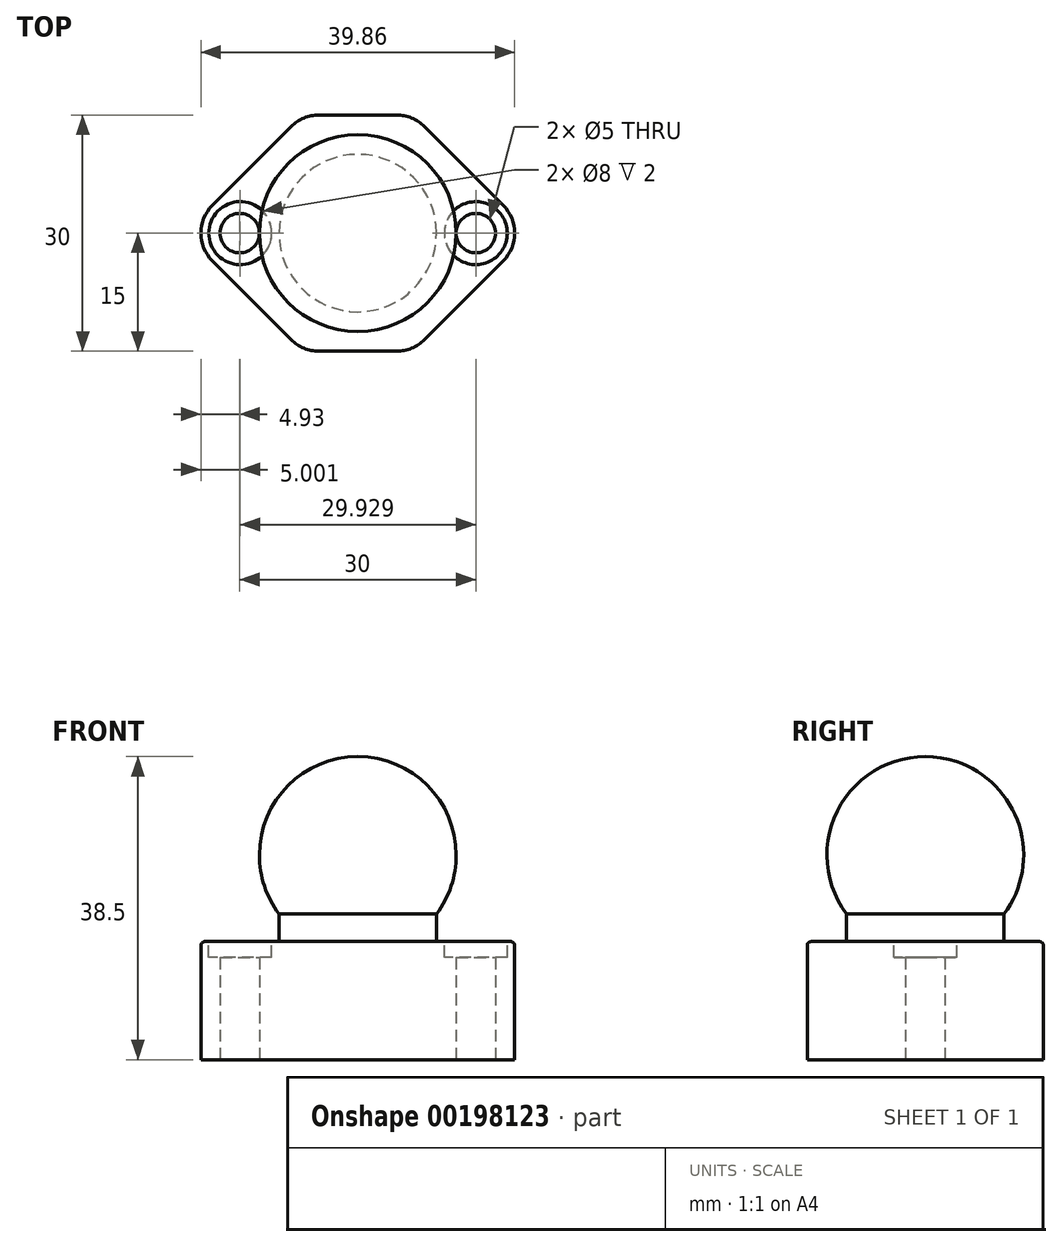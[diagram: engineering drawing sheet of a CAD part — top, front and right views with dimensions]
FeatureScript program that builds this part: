
annotation { "Feature Type Name" : "Feature", "Feature Type Description" : "" }
export const myFeature = defineFeature(function(context is Context, id is Id, definition is map)
    precondition{}
    {
        {
            var Q0;
            Q0=qCreatedBy(makeId("Top.planeOp"),FACE);
            var sketch = newSketch(context, id + "F0", { "sketchPlane" : qUnion([Q0])});
            skCircle(sketch, "E0", {"center": v(0, 0) * mm, "radius": 12.5 * mm});
            skLineSegment(sketch, "E1", {"start": v(22.5, 0) * mm, "end": v(-12.5, 0) * mm});
            skSolve(sketch);
        }
        {
            var Q0;
            {var subQ0=sQuery(id+"F0.wireOp",EDGE,"E1");var subQ1=sQuery(id+"F0.wireOp",EDGE,"E0");var subQ2=makeQuery(id+"F0.imprint","INTERSECT",VERTEX,{"disambiguationData":[OD(0.0)],"derivedFrom":[subQ1,subQ0]});Q0=makeQuery(id+"F0.imprint","IMPRINT",FACE,{"disambiguationData":[TD([[makeQuery(id+"F0.imprint","IMPRINT",EDGE,{"disambiguationData":[TD([[subQ2,1.0]])],"derivedFrom":subQ1}),1.0]])]});}
            var Q1;
            Q1=sQuery(id+"F0.wireOp",EDGE,"E1");
            revolve(context, id + "F1", {"entities" : qUnion([Q0]), "axis" : qUnion([Q1]), "revolveType" : RevolveType.FULL});
        }
        {
            var Q0;
            Q0=qCreatedBy(makeId("Top.planeOp"),FACE);
            var sketch = newSketch(context, id + "F2", { "sketchPlane" : qUnion([Q0])});
            skCircle(sketch, "E2", {"center": v(0, 0) * mm, "radius": 10 * mm});
            skSolve(sketch);
        }
        {
            var Q0;
            Q0 = qSketchRegion(id + "F2", true);
            extrude(context, id + "F3", {"entities" : qUnion([Q0]), "operationType" : NewBodyOperationType.ADD, "oppositeDirection" : true, "depth" : 26 * mm});
        }
        {
            var Q0;
            Q0=makeQuery(id+"F3.opExtrude","CAP_FACE",FACE,{"disambiguationData":[OSD([sQuery(id+"F2.wireOp",EDGE,"E2")])],"isStart":false});
            var sketch = newSketch(context, id + "F4", { "sketchPlane" : qUnion([Q0])});
            skLineSegment(sketch, "E3", {"start": v(0, 15) * mm, "end": v(7, 15) * mm});
            skLineSegment(sketch, "E4", {"start": v(7, 15) * mm, "end": v(22, 0) * mm});
            skLineSegment(sketch, "E5", {"start": v(0, 15) * mm, "end": v(-7, 15) * mm});
            skLineSegment(sketch, "E6", {"start": v(-7, 15) * mm, "end": v(-22, 0) * mm});
            skLineSegment(sketch, "E7", {"start": v(-22, 0) * mm, "end": v(-7, -15) * mm});
            skLineSegment(sketch, "E8", {"start": v(-7, -15) * mm, "end": v(0, -15) * mm});
            skLineSegment(sketch, "E9", {"start": v(7, -15) * mm, "end": v(22, 0) * mm});
            skLineSegment(sketch, "E10", {"start": v(7, -15) * mm, "end": v(0, -15) * mm});
            skCircle(sketch, "E11", {"center": v(15, 0) * mm, "radius": 2.5 * mm});
            skCircle(sketch, "E12", {"center": v(-15, 0) * mm, "radius": 2.5 * mm});
            skSolve(sketch);
        }
        {
            var Q0;
            Q0=makeQuery(id+"F4.imprint","IMPRINT",FACE,{"disambiguationData":[TD([[makeQuery(id+"F4.imprint","IMPRINT",EDGE,{"derivedFrom":sQuery(id+"F4.wireOp",EDGE,"E3")}),-1.0]])]});
            extrude(context, id + "F5", {"entities" : qUnion([Q0]), "operationType" : NewBodyOperationType.ADD, "oppositeDirection" : true, "depth" : 15 * mm});
        }
        {
            var Q0;
            Q0=makeQuery(id+"F5.opExtrude","SWEPT_EDGE",EDGE,{"disambiguationData":[OSD([sQuery(id+"F4.wireOp",EDGE,"E6"),sQuery(id+"F4.wireOp",EDGE,"E7")])]});
            var Q1;
            Q1=makeQuery(id+"F5.opExtrude","SWEPT_EDGE",EDGE,{"disambiguationData":[OSD([sQuery(id+"F4.wireOp",EDGE,"E5"),sQuery(id+"F4.wireOp",EDGE,"E6")])]});
            var Q2;
            Q2=makeQuery(id+"F5.opExtrude","SWEPT_EDGE",EDGE,{"disambiguationData":[OSD([sQuery(id+"F4.wireOp",EDGE,"E3"),sQuery(id+"F4.wireOp",EDGE,"E4")])]});
            var Q3;
            Q3=makeQuery(id+"F5.opExtrude","SWEPT_EDGE",EDGE,{"disambiguationData":[OSD([sQuery(id+"F4.wireOp",EDGE,"E4"),sQuery(id+"F4.wireOp",EDGE,"E9")])]});
            var Q4;
            Q4=makeQuery(id+"F5.opExtrude","SWEPT_EDGE",EDGE,{"disambiguationData":[OSD([sQuery(id+"F4.wireOp",EDGE,"E9"),sQuery(id+"F4.wireOp",EDGE,"E10")])]});
            var Q5;
            Q5=makeQuery(id+"F5.opExtrude","SWEPT_EDGE",EDGE,{"disambiguationData":[OSD([sQuery(id+"F4.wireOp",EDGE,"E7"),sQuery(id+"F4.wireOp",EDGE,"E8")])]});
            fillet(context, id + "F6", {"entities" : qUnion([Q0, Q1, Q2, Q3, Q4, Q5]), "radius" : 5 * mm, "tangentPropagation" : true, "allowEdgeOverflow" : false});
        }
        {
            var Q0;
            Q0=makeQuery(id+"F5.opExtrude","CAP_EDGE",EDGE,{"disambiguationData":[OSD([sQuery(id+"F4.wireOp",EDGE,"E6")])],"isStart":false});
            fillet(context, id + "F7", {"entities" : qUnion([Q0]), "radius" : 0.5 * mm, "tangentPropagation" : true, "allowEdgeOverflow" : false});
        }
        {
            var Q0;
            Q0=makeQuery(id+"F5.opExtrude","CAP_FACE",FACE,{"disambiguationData":[OSD([sQuery(id+"F2.wireOp",EDGE,"E2"),sQuery(id+"F4.wireOp",EDGE,"E3"),sQuery(id+"F4.wireOp",EDGE,"E4"),sQuery(id+"F4.wireOp",EDGE,"E5"),sQuery(id+"F4.wireOp",EDGE,"E6"),sQuery(id+"F4.wireOp",EDGE,"E7"),sQuery(id+"F4.wireOp",EDGE,"E8"),sQuery(id+"F4.wireOp",EDGE,"E9"),sQuery(id+"F4.wireOp",EDGE,"E10"),sQuery(id+"F4.wireOp",EDGE,"E11"),sQuery(id+"F4.wireOp",EDGE,"E12")])],"isStart":false});
            var sketch = newSketch(context, id + "F8", { "sketchPlane" : qUnion([Q0])});
            skCircle(sketch, "E13", {"center": v(-14.93, 0) * mm, "radius": 4 * mm});
            skCircle(sketch, "E14", {"center": v(15, 0) * mm, "radius": 4 * mm});
            skSolve(sketch);
        }
        {
            var Q0;
            Q0=makeQuery(id+"F8.imprint","IMPRINT",FACE,{"disambiguationData":[TD([[makeQuery(id+"F8.imprint","IMPRINT",EDGE,{"derivedFrom":sQuery(id+"F8.wireOp",EDGE,"E13")}),1.0]])]});
            var Q1;
            Q1=makeQuery(id+"F8.imprint","IMPRINT",FACE,{"disambiguationData":[TD([[makeQuery(id+"F8.imprint","IMPRINT",EDGE,{"derivedFrom":sQuery(id+"F8.wireOp",EDGE,"E14")}),1.0]])]});
            extrude(context, id + "F9", {"entities" : qUnion([Q0, Q1]), "operationType" : NewBodyOperationType.REMOVE, "oppositeDirection" : true, "depth" : 2 * mm});
        }
    });
